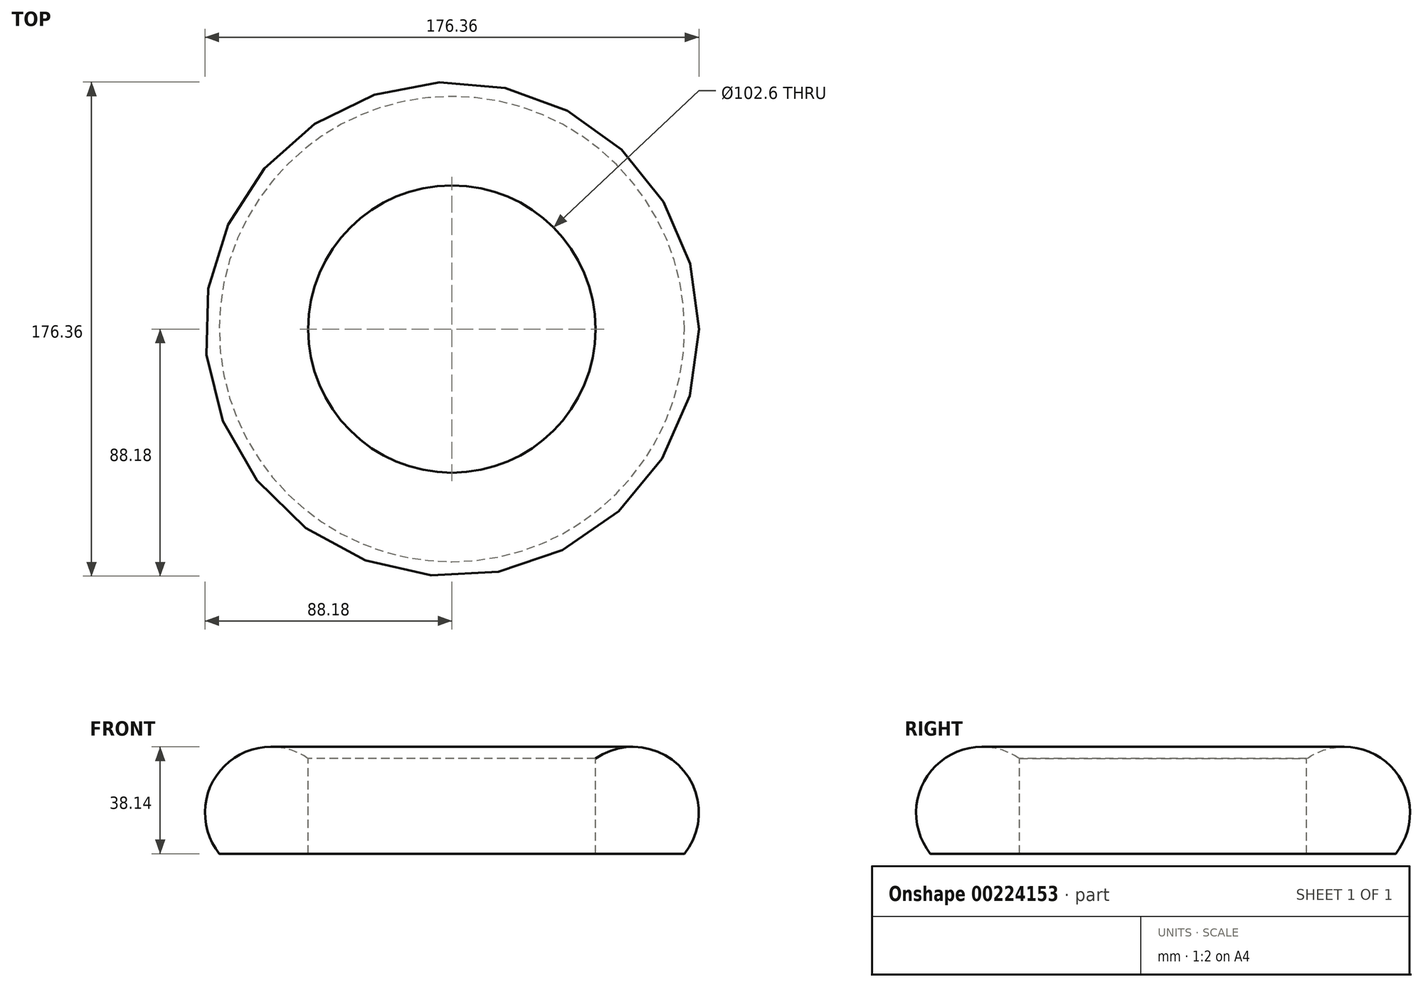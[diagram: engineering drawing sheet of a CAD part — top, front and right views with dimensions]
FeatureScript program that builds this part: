
annotation { "Feature Type Name" : "Feature", "Feature Type Description" : "" }
export const myFeature = defineFeature(function(context is Context, id is Id, definition is map)
    precondition{}
    {
        {
            var Q0;
            Q0=qCreatedBy(makeId("Front.planeOp"),FACE);
            var sketch = newSketch(context, id + "F0", { "sketchPlane" : qUnion([Q0])});
            skLineSegment(sketch, "E0", {"start": v(0, 33.96) * mm, "end": v(0, 0) * mm});
            skLineSegment(sketch, "E1", {"start": v(0, 0) * mm, "end": v(31.77, 0) * mm});
            skArc(sketch, "E2", {"start": v(31.77, 0) * mm, "mid": v(30.54, 30.7) * mm, "end": v(0, 33.96) * mm});
            skLineSegment(sketch, "E3", {"start": v(-51.3, 36.58) * mm, "end": v(-51.3, -34.83) * mm});
            skSolve(sketch);
        }
        {
            var Q0;
            Q0=makeQuery(id+"F0.imprint","IMPRINT",FACE,{"disambiguationData":[TD([[makeQuery(id+"F0.imprint","IMPRINT",EDGE,{"derivedFrom":sQuery(id+"F0.wireOp",EDGE,"E0")}),1.0]])]});
            var Q1;
            Q1=sQuery(id+"F0.wireOp",EDGE,"E3");
            revolve(context, id + "F1", {"entities" : qUnion([Q0]), "axis" : qUnion([Q1]), "revolveType" : RevolveType.FULL});
        }
    });
